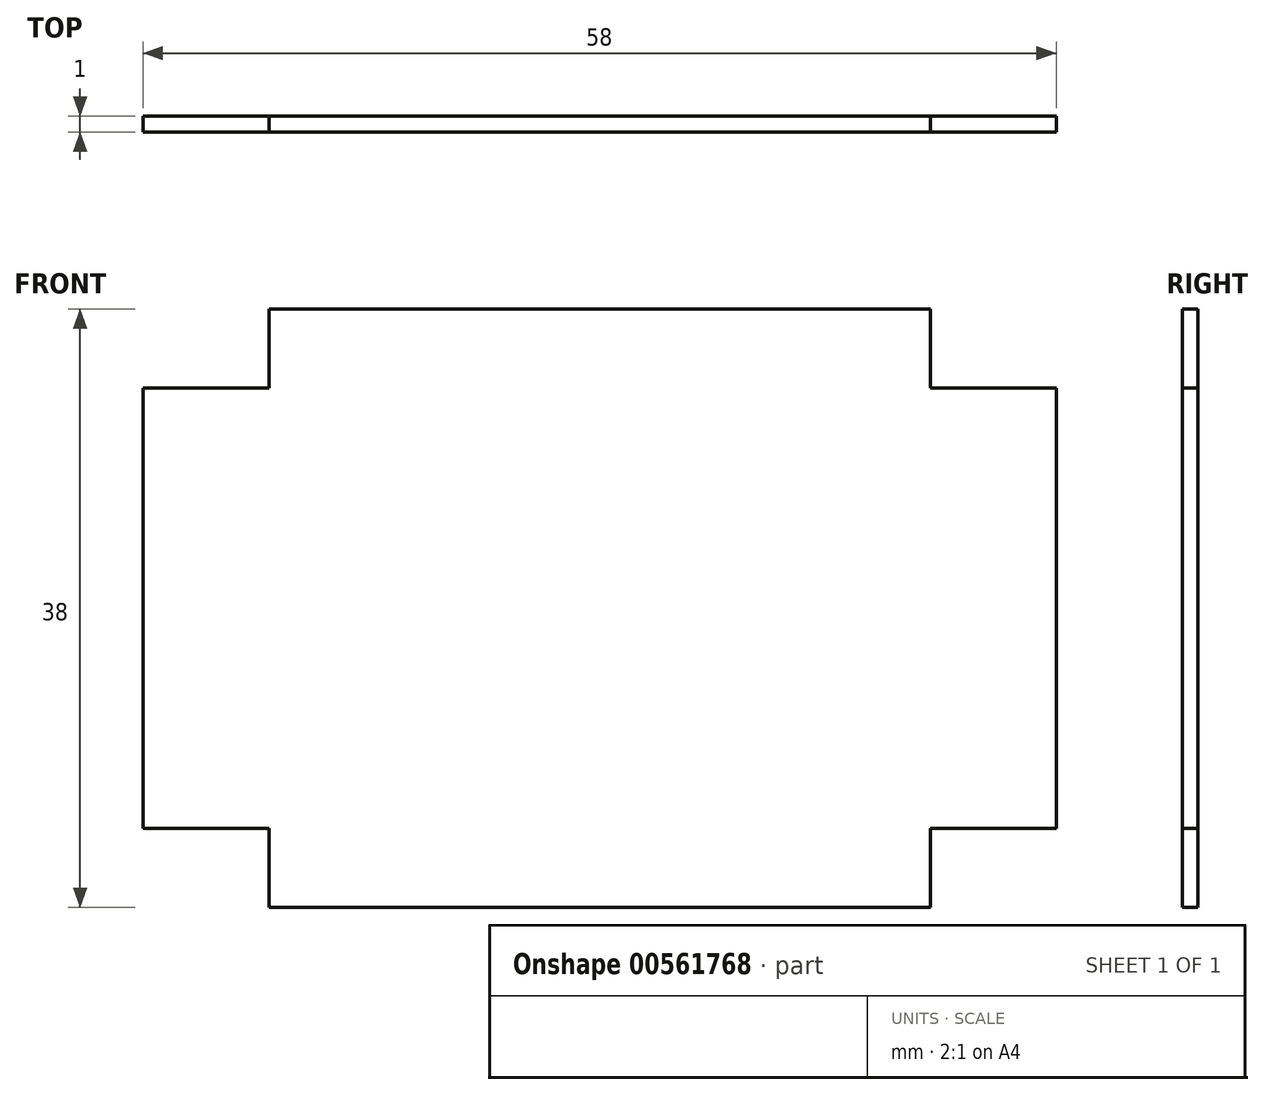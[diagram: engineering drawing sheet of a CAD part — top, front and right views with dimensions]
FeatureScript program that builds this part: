
annotation { "Feature Type Name" : "Feature", "Feature Type Description" : "" }
export const myFeature = defineFeature(function(context is Context, id is Id, definition is map)
    precondition{}
    {
        {
            var Q0;
            Q0=qCreatedBy(makeId("Front.planeOp"),FACE);
            var sketch = newSketch(context, id + "F0", { "sketchPlane" : qUnion([Q0])});
            skLineSegment(sketch, "E0.bottom", {"start": v(-10.5, 19) * mm, "end": v(10.5, 19) * mm});
            skLineSegment(sketch, "E0.top", {"start": v(-10.5, -19) * mm, "end": v(10.5, -19) * mm});
            skLineSegment(sketch, "E0.left", {"start": v(-10.5, 19) * mm, "end": v(-10.5, -19) * mm});
            skLineSegment(sketch, "E0.right", {"start": v(10.5, 19) * mm, "end": v(10.5, -19) * mm});
            skPoint(sketch, "E0.middle", {"position": v(0, 0) * mm});
            skLineSegment(sketch, "E1.MirrorCS", {"start": v(-10.5, 19) * mm, "end": v(-31.5, 19) * mm});
            skLineSegment(sketch, "E2.MirrorCS", {"start": v(-31.5, 19) * mm, "end": v(-31.5, -19) * mm});
            skLineSegment(sketch, "E3.MirrorCS", {"start": v(-10.5, -19) * mm, "end": v(-31.5, -19) * mm});
            skSolve(sketch);
        }
        {
            var Q0;
            Q0 = qSketchRegion(id + "F0", true);
            extrude(context, id + "F1", {"entities" : qUnion([Q0]), "depth" : 1 * mm, "offsetDistance" : 25 * mm});
        }
        {
            var Q0;
            Q0=makeQuery(id+"F1.opExtrude","SWEPT_FACE",FACE,{"disambiguationData":[OSD([sQuery(id+"F0.wireOp",EDGE,"E0.right")])]});
            var sketch = newSketch(context, id + "F2", { "sketchPlane" : qUnion([Q0])});
            skLineSegment(sketch, "E4.bottom", {"start": v(-1, 14) * mm, "end": v(0, 14) * mm});
            skLineSegment(sketch, "E4.top", {"start": v(-1, -14) * mm, "end": v(0, -14) * mm});
            skLineSegment(sketch, "E4.left", {"start": v(-1, 14) * mm, "end": v(-1, -14) * mm});
            skLineSegment(sketch, "E4.right", {"start": v(0, 14) * mm, "end": v(0, -14) * mm});
            skPoint(sketch, "E4.middle", {"position": v(-0.5, 0) * mm});
            skPoint(sketch, "E4.middle.positionSnap0", {"position": v(-1, 0) * mm});
            skPoint(sketch, "E4.middle.positionSnap1", {"position": v(-0.5, -19) * mm});
            skPoint(sketch, "E4.centerSnap0", {"position": v(-1, 0) * mm});
            skPoint(sketch, "E4.centerSnap1", {"position": v(-0.5, -19) * mm});
            skSolve(sketch);
        }
        {
            var Q0;
            Q0 = qSketchRegion(id + "F2", true);
            extrude(context, id + "F3", {"entities" : qUnion([Q0]), "operationType" : NewBodyOperationType.ADD, "depth" : 8 * mm, "offsetDistance" : 25 * mm});
        }
        {
            var Q0;
            Q0=makeQuery(id+"F1.opExtrude","SWEPT_FACE",FACE,{"disambiguationData":[OSD([sQuery(id+"F0.wireOp",EDGE,"E2.MirrorCS")])]});
            var sketch = newSketch(context, id + "F4", { "sketchPlane" : qUnion([Q0])});
            skLineSegment(sketch, "E5.bottom", {"start": v(1, 14) * mm, "end": v(0, 14) * mm});
            skLineSegment(sketch, "E5.top", {"start": v(1, -14) * mm, "end": v(0, -14) * mm});
            skLineSegment(sketch, "E5.left", {"start": v(1, 14) * mm, "end": v(1, -14) * mm});
            skLineSegment(sketch, "E5.right", {"start": v(0, 14) * mm, "end": v(0, -14) * mm});
            skPoint(sketch, "E5.middle", {"position": v(0.5, 0) * mm});
            skPoint(sketch, "E5.middle.positionSnap0", {"position": v(0.5, 19) * mm});
            skPoint(sketch, "E5.centerSnap0", {"position": v(0.5, 19) * mm});
            skSolve(sketch);
        }
        {
            var Q0;
            Q0=makeQuery(id+"F4.imprint","IMPRINT",FACE,{"disambiguationData":[TD([[makeQuery(id+"F4.imprint","IMPRINT",EDGE,{"derivedFrom":sQuery(id+"F4.wireOp",EDGE,"E5.bottom")}),1.0]])]});
            extrude(context, id + "F5", {"entities" : qUnion([Q0]), "operationType" : NewBodyOperationType.ADD, "depth" : 8 * mm, "offsetDistance" : 25 * mm});
        }
    });
